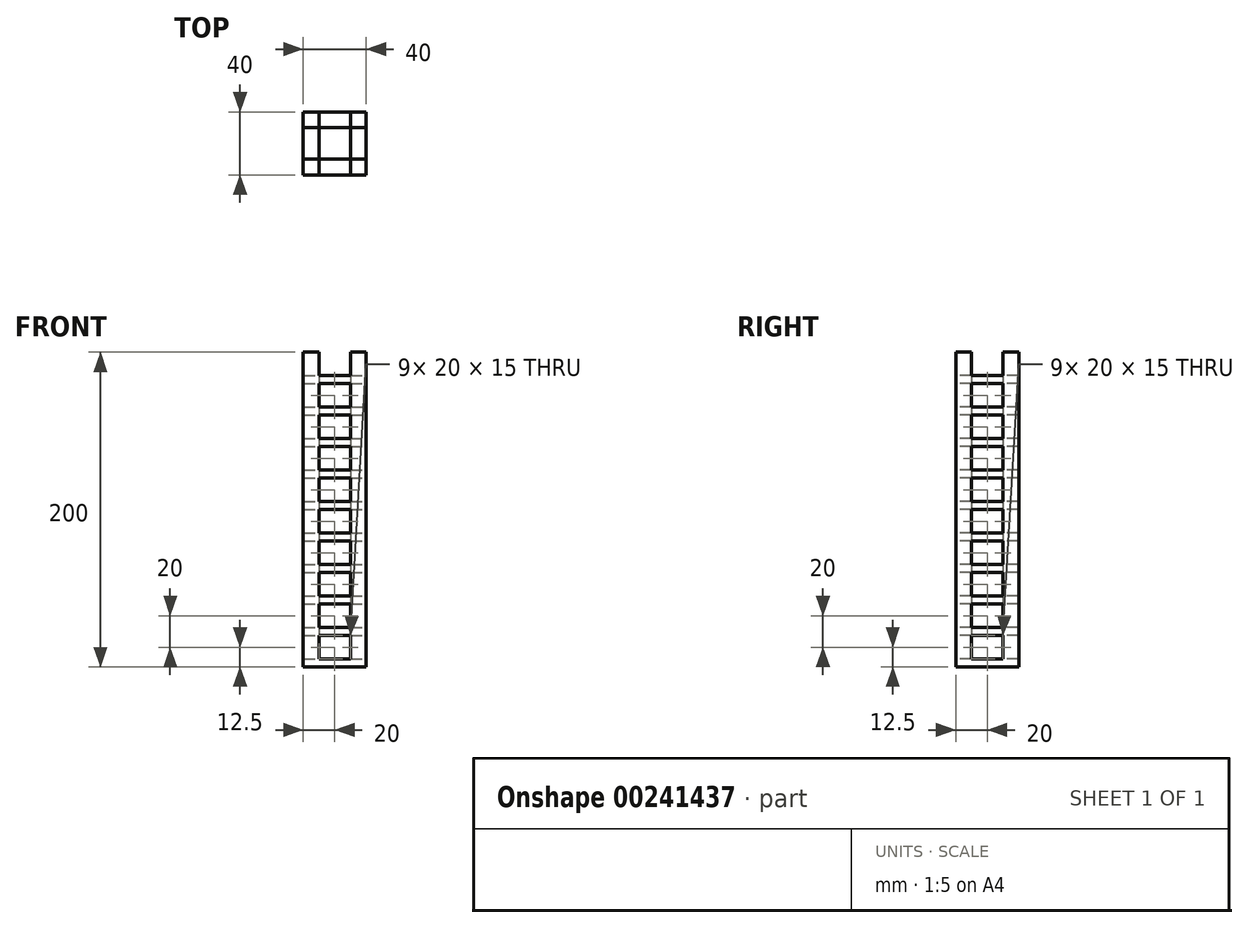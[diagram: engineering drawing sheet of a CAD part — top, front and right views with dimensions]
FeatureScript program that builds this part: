
annotation { "Feature Type Name" : "Feature", "Feature Type Description" : "" }
export const myFeature = defineFeature(function(context is Context, id is Id, definition is map)
    precondition{}
    {
        {
            var Q0;
            Q0=qCreatedBy(makeId("Top.planeOp"),FACE);
            var sketch = newSketch(context, id + "F0", { "sketchPlane" : qUnion([Q0])});
            skLineSegment(sketch, "E0.bottom", {"start": v(-20, 20) * mm, "end": v(20, 20) * mm});
            skLineSegment(sketch, "E0.top", {"start": v(-20, -20) * mm, "end": v(20, -20) * mm});
            skLineSegment(sketch, "E0.left", {"start": v(-20, 20) * mm, "end": v(-20, -20) * mm});
            skLineSegment(sketch, "E0.right", {"start": v(20, 20) * mm, "end": v(20, -20) * mm});
            skPoint(sketch, "E0.middle", {"position": v(0, 0) * mm});
            skSolve(sketch);
        }
        {
            var Q0;
            Q0 = qSketchRegion(id + "F0", true);
            extrude(context, id + "F1", {"entities" : qUnion([Q0]), "depth" : 200 * mm});
        }
        {
            var Q0;
            Q0=makeQuery(id+"F1.opExtrude","SWEPT_FACE",FACE,{"disambiguationData":[OSD([sQuery(id+"F0.wireOp",EDGE,"E0.top")])]});
            var sketch = newSketch(context, id + "F2", { "sketchPlane" : qUnion([Q0])});
            skLineSegment(sketch, "E1.bottom", {"start": v(-10, 5) * mm, "end": v(10, 5) * mm});
            skLineSegment(sketch, "E1.top", {"start": v(-10, 20) * mm, "end": v(10, 20) * mm});
            skLineSegment(sketch, "E1.left", {"start": v(-10, 5) * mm, "end": v(-10, 20) * mm});
            skLineSegment(sketch, "E1.right", {"start": v(10, 5) * mm, "end": v(10, 20) * mm});
            skLineSegment(sketch, "E2.0.1.0", {"start": v(-10, 40) * mm, "end": v(10, 40) * mm});
            skLineSegment(sketch, "E2.0.1.1", {"start": v(-10, 25) * mm, "end": v(-10, 40) * mm});
            skLineSegment(sketch, "E2.0.1.2", {"start": v(-10, 25) * mm, "end": v(10, 25) * mm});
            skLineSegment(sketch, "E2.0.1.3", {"start": v(10, 25) * mm, "end": v(10, 40) * mm});
            skLineSegment(sketch, "E2.0.2.0", {"start": v(-10, 60) * mm, "end": v(10, 60) * mm});
            skLineSegment(sketch, "E2.0.2.1", {"start": v(-10, 45) * mm, "end": v(-10, 60) * mm});
            skLineSegment(sketch, "E2.0.2.2", {"start": v(-10, 45) * mm, "end": v(10, 45) * mm});
            skLineSegment(sketch, "E2.0.2.3", {"start": v(10, 45) * mm, "end": v(10, 60) * mm});
            skLineSegment(sketch, "E2.0.3.0", {"start": v(-10, 80) * mm, "end": v(10, 80) * mm});
            skLineSegment(sketch, "E2.0.3.1", {"start": v(-10, 65) * mm, "end": v(-10, 80) * mm});
            skLineSegment(sketch, "E2.0.3.2", {"start": v(-10, 65) * mm, "end": v(10, 65) * mm});
            skLineSegment(sketch, "E2.0.3.3", {"start": v(10, 65) * mm, "end": v(10, 80) * mm});
            skLineSegment(sketch, "E2.direction1", {"start": v(-10, 20) * mm, "end": v(15, 20) * mm, "construction": true});
            skLineSegment(sketch, "E2.direction2", {"start": v(-10, 20) * mm, "end": v(-10, 40) * mm, "construction": true});
            skLineSegment(sketch, "E3.0.0.4", {"start": v(-10, 100) * mm, "end": v(10, 100) * mm});
            skLineSegment(sketch, "E3.3.0.4", {"start": v(-10, 85) * mm, "end": v(-10, 100) * mm});
            skLineSegment(sketch, "E3.6.0.4", {"start": v(-10, 85) * mm, "end": v(10, 85) * mm});
            skLineSegment(sketch, "E3.9.0.4", {"start": v(10, 85) * mm, "end": v(10, 100) * mm});
            skLineSegment(sketch, "E4.0.0.5", {"start": v(-10, 120) * mm, "end": v(10, 120) * mm});
            skLineSegment(sketch, "E4.3.0.5", {"start": v(-10, 105) * mm, "end": v(-10, 120) * mm});
            skLineSegment(sketch, "E4.6.0.5", {"start": v(-10, 105) * mm, "end": v(10, 105) * mm});
            skLineSegment(sketch, "E4.9.0.5", {"start": v(10, 105) * mm, "end": v(10, 120) * mm});
            skLineSegment(sketch, "E4.0.0.6", {"start": v(-10, 140) * mm, "end": v(10, 140) * mm});
            skLineSegment(sketch, "E4.3.0.6", {"start": v(-10, 125) * mm, "end": v(-10, 140) * mm});
            skLineSegment(sketch, "E4.6.0.6", {"start": v(-10, 125) * mm, "end": v(10, 125) * mm});
            skLineSegment(sketch, "E4.9.0.6", {"start": v(10, 125) * mm, "end": v(10, 140) * mm});
            skLineSegment(sketch, "E5.0.0.7", {"start": v(-10, 160) * mm, "end": v(10, 160) * mm});
            skLineSegment(sketch, "E5.3.0.7", {"start": v(-10, 145) * mm, "end": v(-10, 160) * mm});
            skLineSegment(sketch, "E5.6.0.7", {"start": v(-10, 145) * mm, "end": v(10, 145) * mm});
            skLineSegment(sketch, "E5.9.0.7", {"start": v(10, 145) * mm, "end": v(10, 160) * mm});
            skLineSegment(sketch, "E6.0.0.8", {"start": v(-10, 180) * mm, "end": v(10, 180) * mm});
            skLineSegment(sketch, "E6.3.0.8", {"start": v(-10, 165) * mm, "end": v(-10, 180) * mm});
            skLineSegment(sketch, "E6.6.0.8", {"start": v(-10, 165) * mm, "end": v(10, 165) * mm});
            skLineSegment(sketch, "E6.9.0.8", {"start": v(10, 165) * mm, "end": v(10, 180) * mm});
            skLineSegment(sketch, "E6.0.0.9", {"start": v(-10, 200) * mm, "end": v(10, 200) * mm});
            skLineSegment(sketch, "E6.3.0.9", {"start": v(-10, 185) * mm, "end": v(-10, 200) * mm});
            skLineSegment(sketch, "E6.6.0.9", {"start": v(-10, 185) * mm, "end": v(10, 185) * mm});
            skLineSegment(sketch, "E6.9.0.9", {"start": v(10, 185) * mm, "end": v(10, 200) * mm});
            skSolve(sketch);
        }
        {
            var Q0;
            Q0 = qSketchRegion(id + "F2", true);
            extrude(context, id + "F3", {"entities" : qUnion([Q0]), "operationType" : NewBodyOperationType.REMOVE, "endBound" : BoundingType.THROUGH_ALL, "oppositeDirection" : true, "depth" : 25 * mm});
        }
        {
            var Q0;
            Q0=makeQuery(id+"F1.opExtrude","SWEPT_FACE",FACE,{"disambiguationData":[OSD([sQuery(id+"F0.wireOp",EDGE,"E0.right")])]});
            var sketch = newSketch(context, id + "F4", { "sketchPlane" : qUnion([Q0])});
            skLineSegment(sketch, "E7.bottom", {"start": v(-10, 5) * mm, "end": v(10, 5) * mm});
            skLineSegment(sketch, "E7.top", {"start": v(-10, 20) * mm, "end": v(10, 20) * mm});
            skLineSegment(sketch, "E7.left", {"start": v(-10, 5) * mm, "end": v(-10, 20) * mm});
            skLineSegment(sketch, "E7.right", {"start": v(10, 5) * mm, "end": v(10, 20) * mm});
            skLineSegment(sketch, "E8.0.1.0", {"start": v(-10, 40) * mm, "end": v(10, 40) * mm});
            skLineSegment(sketch, "E8.0.1.1", {"start": v(-10, 25) * mm, "end": v(-10, 40) * mm});
            skLineSegment(sketch, "E8.0.1.2", {"start": v(10, 25) * mm, "end": v(10, 40) * mm});
            skLineSegment(sketch, "E8.0.1.3", {"start": v(-10, 25) * mm, "end": v(10, 25) * mm});
            skLineSegment(sketch, "E8.0.2.0", {"start": v(-10, 60) * mm, "end": v(10, 60) * mm});
            skLineSegment(sketch, "E8.0.2.1", {"start": v(-10, 45) * mm, "end": v(-10, 60) * mm});
            skLineSegment(sketch, "E8.0.2.2", {"start": v(10, 45) * mm, "end": v(10, 60) * mm});
            skLineSegment(sketch, "E8.0.2.3", {"start": v(-10, 45) * mm, "end": v(10, 45) * mm});
            skLineSegment(sketch, "E8.0.3.0", {"start": v(-10, 80) * mm, "end": v(10, 80) * mm});
            skLineSegment(sketch, "E8.0.3.1", {"start": v(-10, 65) * mm, "end": v(-10, 80) * mm});
            skLineSegment(sketch, "E8.0.3.2", {"start": v(10, 65) * mm, "end": v(10, 80) * mm});
            skLineSegment(sketch, "E8.0.3.3", {"start": v(-10, 65) * mm, "end": v(10, 65) * mm});
            skLineSegment(sketch, "E8.direction1", {"start": v(-10, 20) * mm, "end": v(15, 20) * mm, "construction": true});
            skLineSegment(sketch, "E8.direction2", {"start": v(-10, 20) * mm, "end": v(-10, 40) * mm, "construction": true});
            skLineSegment(sketch, "E9.0.0.4", {"start": v(-10, 100) * mm, "end": v(10, 100) * mm});
            skLineSegment(sketch, "E9.3.0.4", {"start": v(-10, 85) * mm, "end": v(-10, 100) * mm});
            skLineSegment(sketch, "E9.6.0.4", {"start": v(10, 85) * mm, "end": v(10, 100) * mm});
            skLineSegment(sketch, "E9.9.0.4", {"start": v(-10, 85) * mm, "end": v(10, 85) * mm});
            skLineSegment(sketch, "E10.0.0.5", {"start": v(-10, 120) * mm, "end": v(10, 120) * mm});
            skLineSegment(sketch, "E10.3.0.5", {"start": v(-10, 105) * mm, "end": v(-10, 120) * mm});
            skLineSegment(sketch, "E10.6.0.5", {"start": v(10, 105) * mm, "end": v(10, 120) * mm});
            skLineSegment(sketch, "E10.9.0.5", {"start": v(-10, 105) * mm, "end": v(10, 105) * mm});
            skLineSegment(sketch, "E10.0.0.6", {"start": v(-10, 140) * mm, "end": v(10, 140) * mm});
            skLineSegment(sketch, "E10.3.0.6", {"start": v(-10, 125) * mm, "end": v(-10, 140) * mm});
            skLineSegment(sketch, "E10.6.0.6", {"start": v(10, 125) * mm, "end": v(10, 140) * mm});
            skLineSegment(sketch, "E10.9.0.6", {"start": v(-10, 125) * mm, "end": v(10, 125) * mm});
            skLineSegment(sketch, "E10.0.0.7", {"start": v(-10, 160) * mm, "end": v(10, 160) * mm});
            skLineSegment(sketch, "E10.3.0.7", {"start": v(-10, 145) * mm, "end": v(-10, 160) * mm});
            skLineSegment(sketch, "E10.6.0.7", {"start": v(10, 145) * mm, "end": v(10, 160) * mm});
            skLineSegment(sketch, "E10.9.0.7", {"start": v(-10, 145) * mm, "end": v(10, 145) * mm});
            skLineSegment(sketch, "E11.0.0.8", {"start": v(-10, 180) * mm, "end": v(10, 180) * mm});
            skLineSegment(sketch, "E11.3.0.8", {"start": v(-10, 165) * mm, "end": v(-10, 180) * mm});
            skLineSegment(sketch, "E11.6.0.8", {"start": v(10, 165) * mm, "end": v(10, 180) * mm});
            skLineSegment(sketch, "E11.9.0.8", {"start": v(-10, 165) * mm, "end": v(10, 165) * mm});
            skLineSegment(sketch, "E11.0.0.9", {"start": v(-10, 200) * mm, "end": v(10, 200) * mm});
            skLineSegment(sketch, "E11.3.0.9", {"start": v(-10, 185) * mm, "end": v(-10, 200) * mm});
            skLineSegment(sketch, "E11.6.0.9", {"start": v(10, 185) * mm, "end": v(10, 200) * mm});
            skLineSegment(sketch, "E11.9.0.9", {"start": v(-10, 185) * mm, "end": v(10, 185) * mm});
            skSolve(sketch);
        }
        {
            var Q0;
            Q0 = qSketchRegion(id + "F4", true);
            extrude(context, id + "F5", {"entities" : qUnion([Q0]), "operationType" : NewBodyOperationType.REMOVE, "endBound" : BoundingType.THROUGH_ALL, "oppositeDirection" : true, "depth" : 25 * mm});
        }
        {
            var Q0;
            Q0=makeQuery(id+"F5.boolean.opBoolean","MERGE",FACE,{"derivedFrom":[makeQuery(id+"F3.boolean.opBoolean","COPY",FACE,{"derivedFrom":makeQuery(id+"F3.opExtrude","SWEPT_FACE",FACE,{"disambiguationData":[OSD([sQuery(id+"F2.wireOp",EDGE,"E1.bottom")])]})}),makeQuery(id+"F5.opExtrude","SWEPT_FACE",FACE,{"disambiguationData":[OSD([sQuery(id+"F4.wireOp",EDGE,"E7.bottom")])]})]});
            var sketch = newSketch(context, id + "F6", { "sketchPlane" : qUnion([Q0])});
            skLineSegment(sketch, "E12.bottom", {"start": v(-10, 10) * mm, "end": v(10, 10) * mm});
            skLineSegment(sketch, "E12.top", {"start": v(-10, -10) * mm, "end": v(10, -10) * mm});
            skLineSegment(sketch, "E12.left", {"start": v(-10, 10) * mm, "end": v(-10, -10) * mm});
            skLineSegment(sketch, "E12.right", {"start": v(10, 10) * mm, "end": v(10, -10) * mm});
            skSolve(sketch);
        }
        {
            var Q0;
            Q0 = qSketchRegion(id + "F6", true);
            extrude(context, id + "F7", {"entities" : qUnion([Q0]), "operationType" : NewBodyOperationType.REMOVE, "endBound" : BoundingType.THROUGH_ALL, "depth" : 25 * mm});
        }
    });
